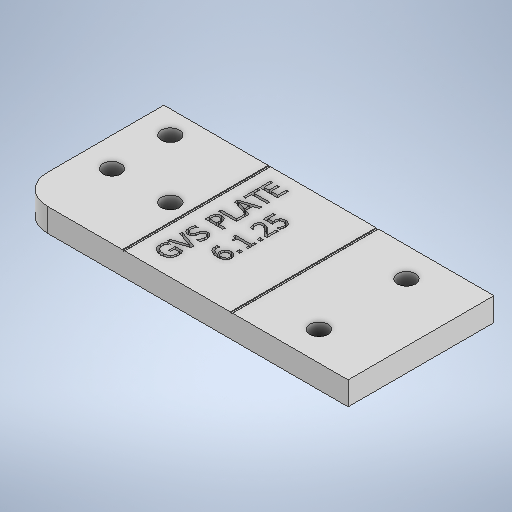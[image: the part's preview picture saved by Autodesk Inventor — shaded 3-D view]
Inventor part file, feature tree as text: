
AUTODESK INVENTOR PART (.ipt)
format: ipt  version: 2025 (Build 290162000, 162)  size: 560,640 bytes
history: native  units: mm
features: sketch x6, extrude x2, fillet x2, emboss x1
ambient origin geometry x8: Origin, YZ Plane, XZ Plane, XY Plane, X Axis, Y Axis, Z Axis, Center Point
bodies: Solid1 (feature_tree)
feature tree (11):
  extrude  "Extrusion1"  Depth=3.9mm
  extrude  "Extrusion2"  Depth=20.0mm
  fillet  "Fillet1"  Radius=25.0mm
  fillet  "Fillet2"  Radius=5.0mm
  emboss  "Emboss1"
  sketch  "Sketch1"  dims[d0=3.1mm d1=3.9mm]
  sketch  "Sketch Rectangular Pattern1"  dims[d2=20.0mm d4=10.0mm d5=10.0mm d7=10.0mm d9=20.0mm d11=10.0mm d12=10.0mm d14=10.0mm d16=25.0mm d17=5.0mm]
  sketch  "Sketch Rectangular Pattern2"  dims[d18=56.58mm]
  sketch  "Sketch Rectangular Pattern3"  dims[d20=10.0mm]
  sketch  "Sketch2"  dims[d19=3.1mm]
  sketch  "Sketch3"  dims[d21=20.0mm d23=15.0mm d24=10.0mm d26=10.0mm d28=5.0mm d29=4.0mm d30=0.0mm d31=0.25mm d32=4.0mm d33=0.0mm d34=18.085mm d35=0.25mm d36=20.0mm d37=0.1mm d38=5.0mm d39=1.0mm d40=0.0mm]
